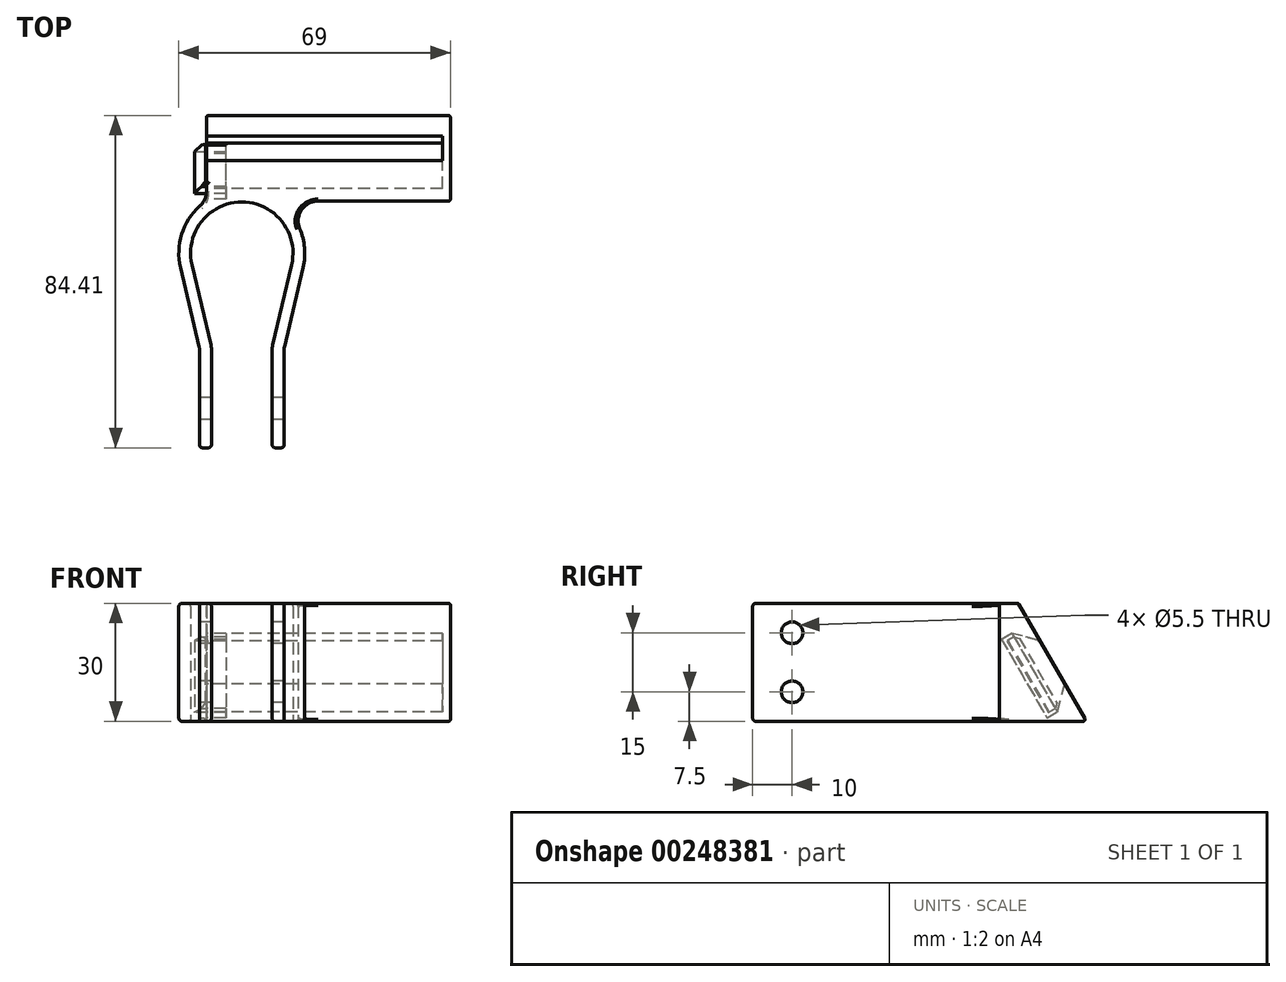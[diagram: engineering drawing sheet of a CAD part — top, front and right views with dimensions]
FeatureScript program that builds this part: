
annotation { "Feature Type Name" : "Feature", "Feature Type Description" : "" }
export const myFeature = defineFeature(function(context is Context, id is Id, definition is map)
    precondition{}
    {
        {
            var Q0;
            Q0=qCreatedBy(makeId("Top.planeOp"),FACE);
            var sketch = newSketch(context, id + "F0", { "sketchPlane" : qUnion([Q0])});
            skCircle(sketch, "E0", {"center": v(0, 23.95) * mm, "radius": 13 * mm});
            skCircle(sketch, "E1", {"center": v(0, 0) * mm, "radius": 7.5 * mm});
            skLineSegment(sketch, "E2", {"start": v(-12.65, 20.97) * mm, "end": v(-7.3, -1.72) * mm});
            skLineSegment(sketch, "E3", {"start": v(7.3, -1.72) * mm, "end": v(12.65, 20.97) * mm});
            skCircle(sketch, "E4", {"center": v(0, 23.95) * mm, "radius": 16 * mm});
            skCircle(sketch, "E5", {"center": v(0, 0) * mm, "radius": 10.5 * mm});
            skLineSegment(sketch, "E6", {"start": v(-15.57, 20.28) * mm, "end": v(-10.22, -2.41) * mm});
            skLineSegment(sketch, "E7", {"start": v(10.22, -2.41) * mm, "end": v(15.57, 20.28) * mm});
            skLineSegment(sketch, "E8", {"start": v(0, 0) * mm, "end": v(0, 39.95) * mm});
            skLineSegment(sketch, "E9", {"start": v(0, 0) * mm, "end": v(0, -10.5) * mm});
            skLineSegment(sketch, "E10", {"start": v(0, 0) * mm, "end": v(-10.79, 0) * mm});
            skLineSegment(sketch, "E11", {"start": v(0, 0) * mm, "end": v(10.79, 0) * mm});
            skPoint(sketch, "E12", {"position": v(0, 39.15) * mm});
            skLineSegment(sketch, "E13", {"start": v(-10.79, 0) * mm, "end": v(-10.79, -25.5) * mm});
            skLineSegment(sketch, "E14", {"start": v(-10.79, -25.5) * mm, "end": v(-7.7, -25.5) * mm});
            skLineSegment(sketch, "E15", {"start": v(-7.7, -25.5) * mm, "end": v(-7.7, 0) * mm});
            skLineSegment(sketch, "E16", {"start": v(7.7, 0) * mm, "end": v(7.7, -25.5) * mm});
            skLineSegment(sketch, "E17", {"start": v(7.7, -25.5) * mm, "end": v(10.79, -25.5) * mm});
            skLineSegment(sketch, "E18", {"start": v(10.79, -25.5) * mm, "end": v(10.79, 0) * mm});
            skSolve(sketch);
        }
        {
            var Q0;
            {var subQ2=sQuery(id+"F0.wireOp",EDGE,"E2");var subQ5=sQuery(id+"F0.wireOp",EDGE,"E0");var subQ8=makeQuery(id+"F0.imprint","INTERSECT",VERTEX,{"derivedFrom":[subQ5,subQ2]});Q0=makeQuery(id+"F0.imprint","IMPRINT",FACE,{"disambiguationData":[TD([[makeQuery(id+"F0.imprint","IMPRINT",EDGE,{"disambiguationData":[TD([[subQ8,1.0]])],"derivedFrom":subQ5}),-1.0]])]});}
            var Q1;
            {var subQ1=sQuery(id+"F0.wireOp",EDGE,"E2");var subQ6=sQuery(id+"F0.wireOp",EDGE,"E4");var subQ9=makeQuery(id+"F0.imprint","INTERSECT",VERTEX,{"derivedFrom":[subQ1,subQ6]});Q1=makeQuery(id+"F0.imprint","IMPRINT",FACE,{"disambiguationData":[TD([[makeQuery(id+"F0.imprint","IMPRINT",EDGE,{"disambiguationData":[TD([[subQ9,-1.0]])],"derivedFrom":subQ1}),-1.0]])]});}
            var Q2;
            {var subQ0=sQuery(id+"F0.wireOp",EDGE,"E5");var subQ1=sQuery(id+"F0.wireOp",EDGE,"E2");var subQ2=makeQuery(id+"F0.imprint","INTERSECT",VERTEX,{"derivedFrom":[subQ1,subQ0]});Q2=makeQuery(id+"F0.imprint","IMPRINT",FACE,{"disambiguationData":[TD([[makeQuery(id+"F0.imprint","IMPRINT",EDGE,{"disambiguationData":[TD([[subQ2,-1.0]])],"derivedFrom":subQ1}),-1.0]])]});}
            var Q3;
            {var subQ4=sQuery(id+"F0.wireOp",EDGE,"E0");var subQ6=sQuery(id+"F0.wireOp",EDGE,"E3");var subQ8=makeQuery(id+"F0.imprint","INTERSECT",VERTEX,{"derivedFrom":[subQ4,subQ6]});Q3=makeQuery(id+"F0.imprint","IMPRINT",FACE,{"disambiguationData":[TD([[makeQuery(id+"F0.imprint","IMPRINT",EDGE,{"disambiguationData":[TD([[subQ8,-1.0]])],"derivedFrom":subQ4}),-1.0]])]});}
            var Q4;
            {var subQ0=sQuery(id+"F0.wireOp",EDGE,"E5");var subQ1=sQuery(id+"F0.wireOp",EDGE,"E3");var subQ2=makeQuery(id+"F0.imprint","INTERSECT",VERTEX,{"derivedFrom":[subQ1,subQ0]});Q4=makeQuery(id+"F0.imprint","IMPRINT",FACE,{"disambiguationData":[TD([[makeQuery(id+"F0.imprint","IMPRINT",EDGE,{"disambiguationData":[TD([[subQ2,-1.0]])],"derivedFrom":subQ1}),-1.0]])]});}
            var Q5;
            {var subQ0=sQuery(id+"F0.wireOp",EDGE,"E11");var subQ1=sQuery(id+"F0.wireOp",EDGE,"E3");var subQ2=makeQuery(id+"F0.imprint","INTERSECT",VERTEX,{"derivedFrom":[subQ1,subQ0]});Q5=makeQuery(id+"F0.imprint","IMPRINT",FACE,{"disambiguationData":[TD([[makeQuery(id+"F0.imprint","IMPRINT",EDGE,{"disambiguationData":[TD([[subQ2,-1.0]])],"derivedFrom":subQ1}),-1.0]])]});}
            var Q6;
            Q6=makeQuery(id+"F0.imprint","IMPRINT",FACE,{"disambiguationData":[TD([[makeQuery(id+"F0.imprint","IMPRINT",EDGE,{"derivedFrom":sQuery(id+"F0.wireOp",EDGE,"9wVvWXiX-Cyzn-rFbb-p7QR-byei5gMzVRPz.bottom")}),-1.0]])]});
            var Q7;
            {var subQ0=sQuery(id+"F0.wireOp",EDGE,"E8");var subQ1=sQuery(id+"F0.wireOp",EDGE,"E4");var subQ2=makeQuery(id+"F0.imprint","INTERSECT",VERTEX,{"disambiguationData":[OD(0.0)],"derivedFrom":[subQ1,subQ0]});Q7=makeQuery(id+"F0.imprint","IMPRINT",FACE,{"disambiguationData":[TD([[makeQuery(id+"F0.imprint","IMPRINT",EDGE,{"disambiguationData":[TD([[subQ2,1.0]])],"derivedFrom":subQ0}),1.0]])]});}
            var Q8;
            {var subQ0=sQuery(id+"F0.wireOp",EDGE,"E8");var subQ1=sQuery(id+"F0.wireOp",EDGE,"E4");var subQ2=makeQuery(id+"F0.imprint","INTERSECT",VERTEX,{"disambiguationData":[OD(0.0)],"derivedFrom":[subQ1,subQ0]});Q8=makeQuery(id+"F0.imprint","IMPRINT",FACE,{"disambiguationData":[TD([[makeQuery(id+"F0.imprint","IMPRINT",EDGE,{"disambiguationData":[TD([[subQ2,1.0]])],"derivedFrom":subQ0}),-1.0]])]});}
            var Q9;
            {var subQ3=sQuery(id+"F0.wireOp",EDGE,"E13");Q9=makeQuery(id+"F0.imprint","IMPRINT",FACE,{"disambiguationData":[TD([[makeQuery(id+"F0.imprint","IMPRINT",EDGE,{"derivedFrom":subQ3}),1.0]])]});}
            var Q10;
            {var subQ0=sQuery(id+"F0.wireOp",EDGE,"E5");var subQ1=makeQuery(id+"F0.imprint","INTERSECT",VERTEX,{"derivedFrom":[subQ0,sQuery(id+"F0.wireOp",EDGE,"E6")]});Q10=makeQuery(id+"F0.imprint","IMPRINT",FACE,{"disambiguationData":[TD([[makeQuery(id+"F0.imprint","IMPRINT",EDGE,{"disambiguationData":[TD([[subQ1,1.0]])],"derivedFrom":subQ0}),1.0]])]});}
            var Q11;
            {var subQ0=sQuery(id+"F0.wireOp",EDGE,"E6");var subQ1=sQuery(id+"F0.wireOp",EDGE,"E5");var subQ2=makeQuery(id+"F0.imprint","INTERSECT",VERTEX,{"derivedFrom":[subQ1,subQ0]});Q11=makeQuery(id+"F0.imprint","IMPRINT",FACE,{"disambiguationData":[TD([[makeQuery(id+"F0.imprint","IMPRINT",EDGE,{"disambiguationData":[TD([[subQ2,1.0]])],"derivedFrom":subQ1}),-1.0]])]});}
            var Q12;
            {var subQ0=sQuery(id+"F0.wireOp",EDGE,"E5");var subQ1=makeQuery(id+"F0.imprint","INTERSECT",VERTEX,{"derivedFrom":[subQ0,sQuery(id+"F0.wireOp",EDGE,"E7")]});Q12=makeQuery(id+"F0.imprint","IMPRINT",FACE,{"disambiguationData":[TD([[makeQuery(id+"F0.imprint","IMPRINT",EDGE,{"disambiguationData":[TD([[subQ1,1.0]])],"derivedFrom":subQ0}),1.0]])]});}
            var Q13;
            {var subQ0=sQuery(id+"F0.wireOp",EDGE,"E7");var subQ1=sQuery(id+"F0.wireOp",EDGE,"E5");var subQ2=makeQuery(id+"F0.imprint","INTERSECT",VERTEX,{"derivedFrom":[subQ1,subQ0]});Q13=makeQuery(id+"F0.imprint","IMPRINT",FACE,{"disambiguationData":[TD([[makeQuery(id+"F0.imprint","IMPRINT",EDGE,{"disambiguationData":[TD([[subQ2,-1.0]])],"derivedFrom":subQ1}),-1.0]])]});}
            var Q14;
            {var subQ0=sQuery(id+"F0.wireOp",EDGE,"E17");Q14=makeQuery(id+"F0.imprint","IMPRINT",FACE,{"disambiguationData":[TD([[makeQuery(id+"F0.imprint","IMPRINT",EDGE,{"derivedFrom":subQ0}),1.0]])]});}
            extrude(context, id + "F1", {"entities" : qUnion([Q0, Q1, Q2, Q3, Q4, Q5, Q6, Q7, Q8, Q9, Q10, Q11, Q12, Q13, Q14]), "depth" : 30 * mm});
        }
        {
            var Q0;
            Q0=qCreatedBy(makeId("Right.planeOp"),FACE);
            var sketch = newSketch(context, id + "F2", { "sketchPlane" : qUnion([Q0])});
            skLineSegment(sketch, "E19", {"start": v(41.95, 30) * mm, "end": v(59.27, 0) * mm});
            skLineSegment(sketch, "E20", {"start": v(59.27, 0) * mm, "end": v(41.95, 0) * mm});
            skLineSegment(sketch, "E21", {"start": v(41.95, 0) * mm, "end": v(41.95, 30) * mm});
            skLineSegment(sketch, "E22", {"start": v(41.95, 30) * mm, "end": v(36.95, 30) * mm});
            skLineSegment(sketch, "E23", {"start": v(41.95, 0) * mm, "end": v(36.95, 0) * mm});
            skLineSegment(sketch, "E24", {"start": v(36.95, 30) * mm, "end": v(36.95, 0) * mm});
            skSolve(sketch);
        }
        {
            var Q0;
            Q0=makeQuery(id+"F2.imprint","IMPRINT",FACE,{"disambiguationData":[TD([[makeQuery(id+"F2.imprint","IMPRINT",EDGE,{"derivedFrom":sQuery(id+"F2.wireOp",EDGE,"E19")}),-1.0]])]});
            var Q1;
            Q1=makeQuery(id+"F2.imprint","IMPRINT",FACE,{"disambiguationData":[TD([[makeQuery(id+"F2.imprint","IMPRINT",EDGE,{"derivedFrom":sQuery(id+"F2.wireOp",EDGE,"E21")}),1.0]])]});
            extrude(context, id + "F3", {"entities" : qUnion([Q0, Q1]), "operationType" : NewBodyOperationType.ADD, "endBound" : BoundingType.SYMMETRIC, "depth" : 18 * mm});
        }
        {
            var Q0;
            Q0=makeQuery(id+"F3.opExtrude","CAP_FACE",FACE,{"disambiguationData":[OSD([sQuery(id+"F2.wireOp",EDGE,"E19"),sQuery(id+"F2.wireOp",EDGE,"E20"),sQuery(id+"F2.wireOp",EDGE,"E21")])],"isStart":true});
            var sketch = newSketch(context, id + "F4", { "sketchPlane" : qUnion([Q0])});
            skLineSegment(sketch, "E25", {"start": v(-47.46, 20.46) * mm, "end": v(-40.36, 22.36) * mm});
            skLineSegment(sketch, "E26", {"start": v(-40.36, 22.36) * mm, "end": v(-51.86, 2.44) * mm});
            skLineSegment(sketch, "E27", {"start": v(-51.86, 2.44) * mm, "end": v(-53.76, 9.54) * mm});
            skLineSegment(sketch, "E28", {"start": v(-53.76, 9.54) * mm, "end": v(-47.46, 20.46) * mm});
            skPoint(sketch, "E29", {"position": v(-50.61, 15) * mm});
            skSolve(sketch);
        }
        {
            var Q0;
            Q0=makeQuery(id+"F3.opExtrude","CAP_FACE",FACE,{"disambiguationData":[OSD([sQuery(id+"F2.wireOp",EDGE,"E19"),sQuery(id+"F2.wireOp",EDGE,"E20"),sQuery(id+"F2.wireOp",EDGE,"E22"),sQuery(id+"F2.wireOp",EDGE,"E23"),sQuery(id+"F2.wireOp",EDGE,"E24")])],"isStart":false});
            extrude(context, id + "F5", {"entities" : qUnion([Q0]), "operationType" : NewBodyOperationType.ADD, "depth" : (60 - 18 + 2) * mm});
        }
        {
            var Q0;
            Q0=makeQuery(id+"F4.imprint","IMPRINT",FACE,{"disambiguationData":[TD([[makeQuery(id+"F4.imprint","IMPRINT",EDGE,{"derivedFrom":sQuery(id+"F4.wireOp",EDGE,"E25")}),-1.0]])]});
            extrude(context, id + "F6", {"entities" : qUnion([Q0]), "operationType" : NewBodyOperationType.REMOVE, "oppositeDirection" : true, "depth" : 60 * mm});
        }
        {
            var Q0;
            Q0=makeQuery(id+"F1.opExtrude","SWEPT_FACE",FACE,{"disambiguationData":[OSD([sQuery(id+"F0.wireOp",EDGE,"E13")])]});
            var sketch = newSketch(context, id + "F7", { "sketchPlane" : qUnion([Q0])});
            skPoint(sketch, "E30", {"position": v(15.5, 22.5) * mm});
            skPoint(sketch, "E31", {"position": v(15.5, 7.5) * mm});
            skLineSegment(sketch, "E32", {"start": v(15.5, 22.5) * mm, "end": v(15.5, 7.5) * mm});
            skPoint(sketch, "E33", {"position": v(15.5, 15) * mm});
            skPoint(sketch, "E34", {"position": v(25.5, 15) * mm});
            skSolve(sketch);
        }
        {
            var Q0;
            Q0=sQuery(id+"F7.wireOp",VERTEX,"E30");
            var Q1;
            Q1=sQuery(id+"F7.wireOp",VERTEX,"E31");
            var Q2;
            Q2=makeQuery(id+"F1.opExtrude","SWEPT_BODY",BODY,{"disambiguationData":[OSD([sQuery(id+"F0.wireOp",EDGE,"E0"),sQuery(id+"F0.wireOp",EDGE,"E2"),sQuery(id+"F0.wireOp",EDGE,"E3"),sQuery(id+"F0.wireOp",EDGE,"E4"),sQuery(id+"F0.wireOp",EDGE,"E6"),sQuery(id+"F0.wireOp",EDGE,"E7"),sQuery(id+"F0.wireOp",EDGE,"E13"),sQuery(id+"F0.wireOp",EDGE,"E14"),sQuery(id+"F0.wireOp",EDGE,"E15"),sQuery(id+"F0.wireOp",EDGE,"E16"),sQuery(id+"F0.wireOp",EDGE,"E17"),sQuery(id+"F0.wireOp",EDGE,"E18")])]});
            hole(context, id + "F8", {"style" : HoleStyle.SIMPLE, "endStyle" : HoleEndStyle.THROUGH, "standardTappedOrClearance" : lookupTablePath({ "standard" : "ISO", "fit" : "Normal", "size" : "M5", "type" : "Clearance" }), "standardBlindInLast" : lookupTablePath({ "fit" : "Standard", "standard" : "ISO", "size" : "M5", "type" : "Clearance" }), "holeDiameter" : 5.5 * mm, "tappedDepth" : 13.2 * mm, "tapClearance" : 3, "startFromSketch" : true, "locations" : qUnion([Q0, Q1]), "scope" : qUnion([Q2])});
        }
        {
            var Q0;
            Q0=makeQuery(id+"F3.opExtrude","CAP_FACE",FACE,{"disambiguationData":[OSD([sQuery(id+"F2.wireOp",EDGE,"E19"),sQuery(id+"F2.wireOp",EDGE,"E20"),sQuery(id+"F2.wireOp",EDGE,"E22"),sQuery(id+"F2.wireOp",EDGE,"E23"),sQuery(id+"F2.wireOp",EDGE,"E24")])],"isStart":true});
            var sketch = newSketch(context, id + "F9", { "sketchPlane" : qUnion([Q0])});
            skLineSegment(sketch, "E35", {"start": v(-40.86, 21.5) * mm, "end": v(-39.1, 20.48) * mm});
            skLineSegment(sketch, "E36", {"start": v(-39.1, 20.48) * mm, "end": v(-49.6, 2.3) * mm});
            skLineSegment(sketch, "E37", {"start": v(-49.6, 2.3) * mm, "end": v(-51.36, 3.3) * mm});
            skLineSegment(sketch, "E38", {"start": v(-40.36, 22.36) * mm, "end": v(-37.74, 20.85) * mm});
            skLineSegment(sketch, "E39", {"start": v(-37.74, 20.85) * mm, "end": v(-49.24, 0.93) * mm});
            skLineSegment(sketch, "E40", {"start": v(-49.24, 0.93) * mm, "end": v(-51.86, 2.44) * mm});
            skSolve(sketch);
        }
        {
            var Q0;
            Q0 = qSketchRegion(id + "F9", true);
            var Q1;
            {var subQ2=sQuery(id+"F9.wireOp",EDGE,"E35");Q1=makeQuery(id+"F9.imprint","IMPRINT",FACE,{"disambiguationData":[TD([[makeQuery(id+"F9.imprint","IMPRINT",EDGE,{"derivedFrom":subQ2}),1.0]])]});}
            extrude(context, id + "F10", {"entities" : qUnion([Q0, Q1]), "operationType" : NewBodyOperationType.REMOVE, "oppositeDirection" : true, "depth" : 5 * mm});
        }
        {
            var Q0;
            Q0=makeQuery(id+"F10.boolean.opBoolean","SPLIT",FACE,{"disambiguationData":[TD([makeQuery(id+"F6.boolean.opBoolean","COPY",FACE,{"derivedFrom":makeQuery(id+"F6.opExtrude","SWEPT_FACE",FACE,{"disambiguationData":[OSD([sQuery(id+"F4.wireOp",EDGE,"E26")])]})})])],"derivedFrom":makeQuery(id+"F3.opExtrude","CAP_FACE",FACE,{"disambiguationData":[OSD([sQuery(id+"F2.wireOp",EDGE,"E19"),sQuery(id+"F2.wireOp",EDGE,"E20"),sQuery(id+"F2.wireOp",EDGE,"E22"),sQuery(id+"F2.wireOp",EDGE,"E23"),sQuery(id+"F2.wireOp",EDGE,"E24")])],"isStart":true})});
            var sketch = newSketch(context, id + "F11", { "sketchPlane" : qUnion([Q0])});
            skLineSegment(sketch, "E41", {"start": v(-40.86, 21.5) * mm, "end": v(-42.22, 21.13) * mm});
            skLineSegment(sketch, "E42", {"start": v(-42.22, 21.13) * mm, "end": v(-51.72, 4.67) * mm});
            skLineSegment(sketch, "E43", {"start": v(-51.72, 4.67) * mm, "end": v(-51.36, 3.3) * mm});
            skLineSegment(sketch, "E44", {"start": v(-51.36, 3.3) * mm, "end": v(-40.86, 21.5) * mm});
            skSolve(sketch);
        }
        {
            var Q0;
            Q0=makeQuery(id+"F11.imprint","IMPRINT",FACE,{"disambiguationData":[TD([[makeQuery(id+"F11.imprint","IMPRINT",EDGE,{"derivedFrom":sQuery(id+"F11.wireOp",EDGE,"E41")}),1.0]])]});
            var Q1;
            Q1=makeQuery(id+"F11.imprint","IMPRINT",FACE,{"disambiguationData":[TD([[makeQuery(id+"F11.imprint","IMPRINT",EDGE,{"derivedFrom":sQuery(id+"F11.wireOp",EDGE,"E44")}),1.0]])]});
            extrude(context, id + "F12", {"entities" : qUnion([Q0, Q1]), "operationType" : NewBodyOperationType.ADD, "depth" : 3 * mm});
        }
        {
            var Q0;
            Q0=makeQuery(id+"F12.opExtrude","CAP_EDGE",EDGE,{"disambiguationData":[OSD([sQuery(id+"F11.wireOp",EDGE,"E42")])],"isStart":false});
            chamfer(context, id + "F13", {"entities" : qUnion([Q0]), "width" : 2.8 * mm, "tangentPropagation" : true});
        }
        {
            var Q0;
            Q0=makeQuery(id+"F6.boolean.opBoolean","COPY",EDGE,{"derivedFrom":makeQuery(id+"F6.opExtrude","SWEPT_EDGE",EDGE,{"disambiguationData":[OSD([sQuery(id+"F2.wireOp",EDGE,"E19"),sQuery(id+"F4.wireOp",EDGE,"E27"),sQuery(id+"F4.wireOp",EDGE,"E28")])]})});
            var Q1;
            Q1=makeQuery(id+"F6.boolean.opBoolean","COPY",EDGE,{"derivedFrom":makeQuery(id+"F6.opExtrude","SWEPT_EDGE",EDGE,{"disambiguationData":[OSD([sQuery(id+"F2.wireOp",EDGE,"E19"),sQuery(id+"F4.wireOp",EDGE,"E25"),sQuery(id+"F4.wireOp",EDGE,"E28")])]})});
            var Q2;
            Q2=makeQuery(id+"F6.boolean.opBoolean","COPY",EDGE,{"derivedFrom":makeQuery(id+"F6.opExtrude","CAP_EDGE",EDGE,{"disambiguationData":[OSD([sQuery(id+"F4.wireOp",EDGE,"E28")])],"isStart":false})});
            var Q3;
            {var subQ0=sQuery(id+"F2.wireOp",EDGE,"E20");var subQ1=sQuery(id+"F2.wireOp",EDGE,"E19");Q3=makeQuery(id+"F5.boolean.opBoolean","MERGE",EDGE,{"derivedFrom":[makeQuery(id+"F3.opExtrude","SWEPT_EDGE",EDGE,{"disambiguationData":[OSD([subQ1,subQ0])]}),makeQuery(id+"F5.opExtrude","SWEPT_EDGE",EDGE,{"disambiguationData":[OSD([subQ1,subQ0])]})]});}
            var Q4;
            {var subQ0=sQuery(id+"F2.wireOp",EDGE,"E22");var subQ1=sQuery(id+"F2.wireOp",EDGE,"E21");var subQ2=sQuery(id+"F2.wireOp",EDGE,"E19");Q4=makeQuery(id+"F5.boolean.opBoolean","MERGE",EDGE,{"derivedFrom":[makeQuery(id+"F3.opExtrude","SWEPT_EDGE",EDGE,{"disambiguationData":[OSD([subQ2,subQ1,subQ0])]}),makeQuery(id+"F5.opExtrude","SWEPT_EDGE",EDGE,{"disambiguationData":[OSD([subQ2,subQ1,subQ0])]})]});}
            var Q5;
            Q5=makeQuery(id+"F5.opExtrude","CAP_EDGE",EDGE,{"disambiguationData":[OSD([sQuery(id+"F2.wireOp",EDGE,"E19")])],"isStart":false});
            var Q6;
            Q6=makeQuery(id+"F5.opExtrude","CAP_EDGE",EDGE,{"disambiguationData":[OSD([sQuery(id+"F2.wireOp",EDGE,"E20"),sQuery(id+"F2.wireOp",EDGE,"E23")])],"isStart":false});
            var Q7;
            Q7=makeQuery(id+"F5.opExtrude","CAP_EDGE",EDGE,{"disambiguationData":[OSD([sQuery(id+"F0.wireOp",EDGE,"E4"),sQuery(id+"F2.wireOp",EDGE,"E19"),sQuery(id+"F2.wireOp",EDGE,"E20"),sQuery(id+"F2.wireOp",EDGE,"E22"),sQuery(id+"F2.wireOp",EDGE,"E23"),sQuery(id+"F2.wireOp",EDGE,"E24")])],"isStart":false});
            var Q8;
            Q8=makeQuery(id+"F5.opExtrude","CAP_EDGE",EDGE,{"disambiguationData":[OSD([sQuery(id+"F2.wireOp",EDGE,"E22")])],"isStart":false});
            var Q9;
            {var subQ2=sQuery(id+"F2.wireOp",EDGE,"E19");Q9=makeQuery(id+"F6.boolean.opBoolean","SPLIT",EDGE,{"disambiguationData":[TD([makeQuery(id+"F6.opExtrude","SWEPT_FACE",FACE,{"disambiguationData":[OSD([sQuery(id+"F4.wireOp",EDGE,"E27")])]})])],"derivedFrom":makeQuery(id+"F3.opExtrude","CAP_EDGE",EDGE,{"disambiguationData":[OSD([subQ2])],"isStart":true})});}
            var Q10;
            {var subQ0=sQuery(id+"F2.wireOp",EDGE,"E22");var subQ1=sQuery(id+"F2.wireOp",EDGE,"E19");Q10=makeQuery(id+"F6.boolean.opBoolean","SPLIT",EDGE,{"disambiguationData":[TD([makeQuery(id+"F3.opExtrude","SWEPT_FACE",FACE,{"disambiguationData":[OSD([subQ0])]})])],"derivedFrom":makeQuery(id+"F3.opExtrude","CAP_EDGE",EDGE,{"disambiguationData":[OSD([subQ1])],"isStart":true})});}
            var Q11;
            Q11=makeQuery(id+"F3.opExtrude","CAP_EDGE",EDGE,{"disambiguationData":[OSD([sQuery(id+"F2.wireOp",EDGE,"E20"),sQuery(id+"F2.wireOp",EDGE,"E23")])],"isStart":true});
            var Q12;
            Q12=makeQuery(id+"F3.opExtrude","CAP_EDGE",EDGE,{"disambiguationData":[OSD([sQuery(id+"F2.wireOp",EDGE,"E22")])],"isStart":true});
            var Q13;
            {var subQ0=sQuery(id+"F2.wireOp",EDGE,"E24");var subQ1=sQuery(id+"F2.wireOp",EDGE,"E23");var subQ2=sQuery(id+"F2.wireOp",EDGE,"E22");var subQ3=sQuery(id+"F2.wireOp",EDGE,"E20");var subQ4=sQuery(id+"F2.wireOp",EDGE,"E19");var subQ5=sQuery(id+"F0.wireOp",EDGE,"E4");Q13=makeQuery(id+"F5.opExtrude","SWEPT_EDGE",EDGE,{"disambiguationData":[OSD([subQ5,subQ4,subQ3,subQ2,subQ1,subQ0]),TDD([makeQuery(id+"F3.boolean.opBoolean","INTERSECT",VERTEX,{"disambiguationData":[OD(1.0)],"derivedFrom":[makeQuery(id+"F1.opExtrude","SWEPT_FACE",FACE,{"disambiguationData":[OSD([subQ5])]}),makeQuery(id+"F3.opExtrude","CAP_FACE",FACE,{"disambiguationData":[OSD([subQ4,subQ3,subQ2,subQ1,subQ0])],"isStart":false})]})])]});}
            var Q14;
            {var subQ0=sQuery(id+"F2.wireOp",EDGE,"E24");var subQ1=sQuery(id+"F2.wireOp",EDGE,"E23");var subQ2=sQuery(id+"F2.wireOp",EDGE,"E22");var subQ3=sQuery(id+"F2.wireOp",EDGE,"E20");var subQ4=sQuery(id+"F2.wireOp",EDGE,"E19");var subQ5=sQuery(id+"F0.wireOp",EDGE,"E4");Q14=makeQuery(id+"F5.opExtrude","SWEPT_EDGE",EDGE,{"disambiguationData":[OSD([subQ5,subQ4,subQ3,subQ2,subQ1,subQ0]),TDD([makeQuery(id+"F3.boolean.opBoolean","INTERSECT",VERTEX,{"disambiguationData":[OD(0.0)],"derivedFrom":[makeQuery(id+"F1.opExtrude","SWEPT_FACE",FACE,{"disambiguationData":[OSD([subQ5])]}),makeQuery(id+"F3.opExtrude","CAP_FACE",FACE,{"disambiguationData":[OSD([subQ4,subQ3,subQ2,subQ1,subQ0])],"isStart":false})]})])]});}
            fillet(context, id + "F14", {"entities" : qUnion([Q0, Q1, Q2, Q3, Q4, Q5, Q6, Q7, Q8, Q9, Q10, Q11, Q12, Q13, Q14]), "radius" : 0.5 * mm, "tangentPropagation" : true, "allowEdgeOverflow" : false});
        }
        {
            var Q0;
            {var subQ0=sQuery(id+"F2.wireOp",EDGE,"E24");var subQ1=sQuery(id+"F2.wireOp",EDGE,"E23");var subQ2=sQuery(id+"F2.wireOp",EDGE,"E22");var subQ3=sQuery(id+"F2.wireOp",EDGE,"E20");var subQ4=sQuery(id+"F2.wireOp",EDGE,"E19");var subQ5=sQuery(id+"F0.wireOp",EDGE,"E4");Q0=makeQuery(id+"F5.boolean.opBoolean","MERGE",EDGE,{"derivedFrom":[makeQuery(id+"F3.boolean.opBoolean","INTERSECT",EDGE,{"derivedFrom":[makeQuery(id+"F1.opExtrude","SWEPT_FACE",FACE,{"disambiguationData":[OSD([subQ5])]}),makeQuery(id+"F3.opExtrude","CAP_FACE",FACE,{"disambiguationData":[OSD([subQ4,subQ3,subQ2,subQ1,subQ0])],"isStart":false})]}),makeQuery(id+"F5.opExtrude","CAP_EDGE",EDGE,{"disambiguationData":[OSD([subQ5,subQ4,subQ3,subQ2,subQ1,subQ0])],"isStart":true})]});}
            var Q1;
            Q1=makeQuery(id+"F3.boolean.opBoolean","INTERSECT",EDGE,{"derivedFrom":[makeQuery(id+"F1.opExtrude","SWEPT_FACE",FACE,{"disambiguationData":[OSD([sQuery(id+"F0.wireOp",EDGE,"E4")])]}),makeQuery(id+"F3.opExtrude","CAP_FACE",FACE,{"disambiguationData":[OSD([sQuery(id+"F2.wireOp",EDGE,"E19"),sQuery(id+"F2.wireOp",EDGE,"E20"),sQuery(id+"F2.wireOp",EDGE,"E22"),sQuery(id+"F2.wireOp",EDGE,"E23"),sQuery(id+"F2.wireOp",EDGE,"E24")])],"isStart":true})]});
            var Q2;
            Q2=makeQuery(id+"F1.opExtrude","SWEPT_EDGE",EDGE,{"disambiguationData":[OSD([sQuery(id+"F0.wireOp",EDGE,"E3"),sQuery(id+"F0.wireOp",EDGE,"E11"),sQuery(id+"F0.wireOp",EDGE,"E16")])]});
            var Q3;
            Q3=makeQuery(id+"F1.opExtrude","SWEPT_EDGE",EDGE,{"disambiguationData":[OSD([sQuery(id+"F0.wireOp",EDGE,"E2"),sQuery(id+"F0.wireOp",EDGE,"E10"),sQuery(id+"F0.wireOp",EDGE,"E15")])]});
            fillet(context, id + "F15", {"entities" : qUnion([Q0, Q1, Q2, Q3]), "radius" : 5 * mm, "tangentPropagation" : true, "allowEdgeOverflow" : false});
        }
        {
            var Q0;
            Q0=makeQuery(id+"F1.opExtrude","CAP_EDGE",EDGE,{"disambiguationData":[OSD([sQuery(id+"F0.wireOp",EDGE,"E0")])],"isStart":false});
            var Q1;
            Q1=makeQuery(id+"F1.opExtrude","CAP_EDGE",EDGE,{"disambiguationData":[OSD([sQuery(id+"F0.wireOp",EDGE,"E6")])],"isStart":false});
            var Q2;
            Q2=makeQuery(id+"F1.opExtrude","CAP_EDGE",EDGE,{"disambiguationData":[OSD([sQuery(id+"F0.wireOp",EDGE,"E7")])],"isStart":false});
            var Q3;
            Q3=makeQuery(id+"F1.opExtrude","CAP_EDGE",EDGE,{"disambiguationData":[OSD([sQuery(id+"F0.wireOp",EDGE,"E18")])],"isStart":false});
            var Q4;
            Q4=makeQuery(id+"F1.opExtrude","CAP_EDGE",EDGE,{"disambiguationData":[OSD([sQuery(id+"F0.wireOp",EDGE,"E13")])],"isStart":false});
            var Q5;
            {var subQ0=sQuery(id+"F0.wireOp",EDGE,"E7");var subQ3=sQuery(id+"F0.wireOp",EDGE,"E4");Q5=makeQuery(id+"F3.boolean.opBoolean","SPLIT",EDGE,{"disambiguationData":[TD([makeQuery(id+"F1.opExtrude","SWEPT_FACE",FACE,{"disambiguationData":[OSD([subQ0])]})])],"derivedFrom":makeQuery(id+"F1.opExtrude","CAP_EDGE",EDGE,{"disambiguationData":[OSD([subQ3])],"isStart":true})});}
            var Q6;
            Q6=makeQuery(id+"F1.opExtrude","CAP_EDGE",EDGE,{"disambiguationData":[OSD([sQuery(id+"F0.wireOp",EDGE,"E18")])],"isStart":true});
            var Q7;
            Q7=makeQuery(id+"F1.opExtrude","CAP_EDGE",EDGE,{"disambiguationData":[OSD([sQuery(id+"F0.wireOp",EDGE,"E16")])],"isStart":true});
            var Q8;
            Q8=makeQuery(id+"F1.opExtrude","CAP_EDGE",EDGE,{"disambiguationData":[OSD([sQuery(id+"F0.wireOp",EDGE,"E3")])],"isStart":true});
            var Q9;
            Q9=makeQuery(id+"F1.opExtrude","CAP_EDGE",EDGE,{"disambiguationData":[OSD([sQuery(id+"F0.wireOp",EDGE,"E13")])],"isStart":true});
            var Q10;
            Q10=makeQuery(id+"F1.opExtrude","CAP_EDGE",EDGE,{"disambiguationData":[OSD([sQuery(id+"F0.wireOp",EDGE,"E6")])],"isStart":true});
            var Q11;
            Q11=makeQuery(id+"F1.opExtrude","SWEPT_EDGE",EDGE,{"disambiguationData":[OSD([sQuery(id+"F0.wireOp",EDGE,"E6"),sQuery(id+"F0.wireOp",EDGE,"E10"),sQuery(id+"F0.wireOp",EDGE,"E13")])]});
            var Q12;
            Q12=makeQuery(id+"F1.opExtrude","SWEPT_EDGE",EDGE,{"disambiguationData":[OSD([sQuery(id+"F0.wireOp",EDGE,"E7"),sQuery(id+"F0.wireOp",EDGE,"E11"),sQuery(id+"F0.wireOp",EDGE,"E18")])]});
            var Q13;
            Q13=makeQuery(id+"F1.opExtrude","SWEPT_EDGE",EDGE,{"disambiguationData":[OSD([sQuery(id+"F0.wireOp",EDGE,"E17"),sQuery(id+"F0.wireOp",EDGE,"E18")])]});
            var Q14;
            Q14=makeQuery(id+"F1.opExtrude","SWEPT_EDGE",EDGE,{"disambiguationData":[OSD([sQuery(id+"F0.wireOp",EDGE,"E16"),sQuery(id+"F0.wireOp",EDGE,"E17")])]});
            var Q15;
            Q15=makeQuery(id+"F1.opExtrude","SWEPT_EDGE",EDGE,{"disambiguationData":[OSD([sQuery(id+"F0.wireOp",EDGE,"E14"),sQuery(id+"F0.wireOp",EDGE,"E15")])]});
            var Q16;
            Q16=makeQuery(id+"F1.opExtrude","CAP_EDGE",EDGE,{"disambiguationData":[OSD([sQuery(id+"F0.wireOp",EDGE,"E17")])],"isStart":true});
            var Q17;
            Q17=makeQuery(id+"F1.opExtrude","CAP_EDGE",EDGE,{"disambiguationData":[OSD([sQuery(id+"F0.wireOp",EDGE,"E17")])],"isStart":false});
            var Q18;
            Q18=makeQuery(id+"F1.opExtrude","CAP_EDGE",EDGE,{"disambiguationData":[OSD([sQuery(id+"F0.wireOp",EDGE,"E14")])],"isStart":false});
            var Q19;
            Q19=makeQuery(id+"F1.opExtrude","CAP_EDGE",EDGE,{"disambiguationData":[OSD([sQuery(id+"F0.wireOp",EDGE,"E14")])],"isStart":true});
            var Q20;
            Q20=makeQuery(id+"F1.opExtrude","SWEPT_EDGE",EDGE,{"disambiguationData":[OSD([sQuery(id+"F0.wireOp",EDGE,"E13"),sQuery(id+"F0.wireOp",EDGE,"E14")])]});
            fillet(context, id + "F16", {"entities" : qUnion([Q0, Q1, Q2, Q3, Q4, Q5, Q6, Q7, Q8, Q9, Q10, Q11, Q12, Q13, Q14, Q15, Q16, Q17, Q18, Q19, Q20]), "radius" : 0.8 * mm, "tangentPropagation" : true, "allowEdgeOverflow" : false});
        }
    });
